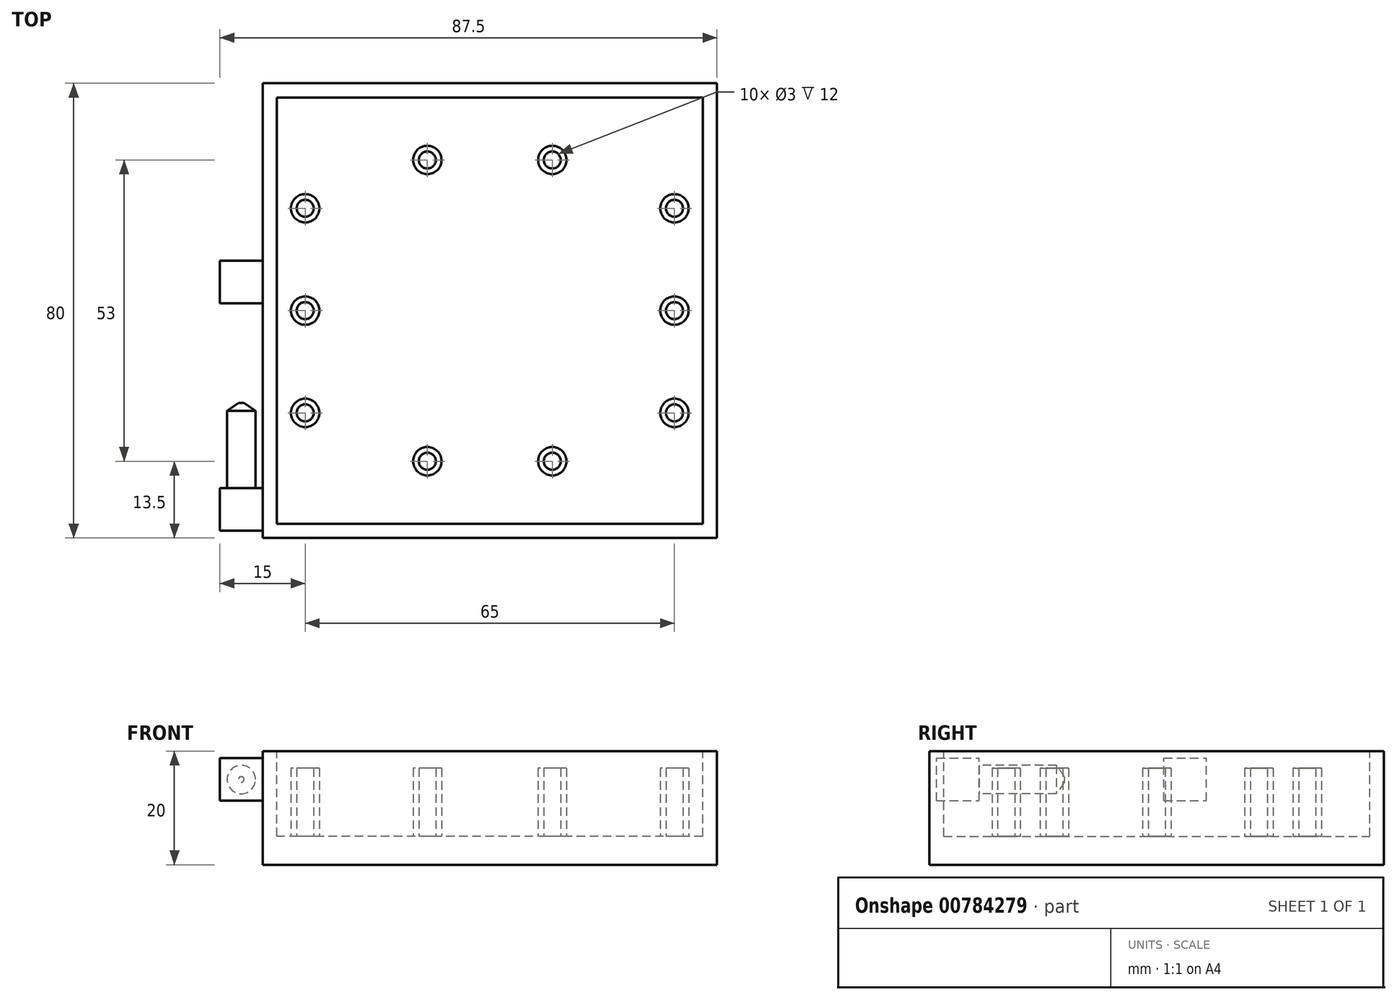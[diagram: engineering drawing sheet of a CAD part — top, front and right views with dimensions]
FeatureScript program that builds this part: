
annotation { "Feature Type Name" : "Feature", "Feature Type Description" : "" }
export const myFeature = defineFeature(function(context is Context, id is Id, definition is map)
    precondition{}
    {
        {
            var Q0;
            Q0=qCreatedBy(makeId("Top.planeOp"),FACE);
            var sketch = newSketch(context, id + "F0", { "sketchPlane" : qUnion([Q0])});
            skLineSegment(sketch, "E0.bottom", {"start": v(-40, -40) * mm, "end": v(40, -40) * mm});
            skLineSegment(sketch, "E0.top", {"start": v(-40, 40) * mm, "end": v(40, 40) * mm});
            skLineSegment(sketch, "E0.left", {"start": v(-40, -40) * mm, "end": v(-40, 40) * mm});
            skLineSegment(sketch, "E0.right", {"start": v(40, -40) * mm, "end": v(40, 40) * mm});
            skPoint(sketch, "E0.middle", {"position": v(0, 0) * mm});
            skSolve(sketch);
        }
        {
            var Q0;
            Q0=makeQuery(id+"F0.imprint","IMPRINT",FACE,{"disambiguationData":[TD([[makeQuery(id+"F0.imprint","IMPRINT",EDGE,{"derivedFrom":sQuery(id+"F0.wireOp",EDGE,"E0.bottom")}),1.0]])]});
            extrude(context, id + "F1", {"entities" : qUnion([Q0]), "depth" : 20 * mm, "offsetDistance" : 25 * mm});
        }
        {
            var Q0;
            Q0=makeQuery(id+"F1.opExtrude","CAP_FACE",FACE,{"disambiguationData":[OSD([sQuery(id+"F0.wireOp",EDGE,"E0.bottom"),sQuery(id+"F0.wireOp",EDGE,"E0.top"),sQuery(id+"F0.wireOp",EDGE,"E0.left"),sQuery(id+"F0.wireOp",EDGE,"E0.right")])],"isStart":false});
            var sketch = newSketch(context, id + "F2", { "sketchPlane" : qUnion([Q0])});
            skLineSegment(sketch, "E1.bottom", {"start": v(37.5, -37.5) * mm, "end": v(-37.5, -37.5) * mm});
            skLineSegment(sketch, "E1.top", {"start": v(37.5, 37.5) * mm, "end": v(-37.5, 37.5) * mm});
            skLineSegment(sketch, "E1.left", {"start": v(37.5, -37.5) * mm, "end": v(37.5, 37.5) * mm});
            skLineSegment(sketch, "E1.right", {"start": v(-37.5, -37.5) * mm, "end": v(-37.5, 37.5) * mm});
            skPoint(sketch, "E1.middle", {"position": v(0, 0) * mm});
            skSolve(sketch);
        }
        {
            var Q0;
            Q0=makeQuery(id+"F2.imprint","IMPRINT",FACE,{"disambiguationData":[TD([[makeQuery(id+"F2.imprint","IMPRINT",EDGE,{"derivedFrom":sQuery(id+"F2.wireOp",EDGE,"E1.bottom")}),-1.0]])]});
            extrude(context, id + "F3", {"entities" : qUnion([Q0]), "operationType" : NewBodyOperationType.REMOVE, "depth" : -15 * mm, "offsetDistance" : 25 * mm});
        }
        {
            var Q0;
            Q0=makeQuery(id+"F3.boolean.opBoolean","COPY",FACE,{"derivedFrom":makeQuery(id+"F3.opExtrude","CAP_FACE",FACE,{"disambiguationData":[OSD([sQuery(id+"F2.wireOp",EDGE,"E1.bottom"),sQuery(id+"F2.wireOp",EDGE,"E1.top"),sQuery(id+"F2.wireOp",EDGE,"E1.left"),sQuery(id+"F2.wireOp",EDGE,"E1.right")])],"isStart":false})});
            var sketch = newSketch(context, id + "F4", { "sketchPlane" : qUnion([Q0])});
            skLineSegment(sketch, "E2", {"start": v(-66.36, -26.5) * mm, "end": v(65.7, -26.5) * mm, "construction": true});
            skLineSegment(sketch, "E3", {"start": v(-32.5, -44) * mm, "end": v(-32.5, 44) * mm, "construction": true});
            skLineSegment(sketch, "E4", {"start": v(32.5, 44.96) * mm, "end": v(32.5, -44) * mm, "construction": true});
            skLineSegment(sketch, "E5", {"start": v(47.78, 26.5) * mm, "end": v(-45.97, 26.5) * mm, "construction": true});
            skCircle(sketch, "E6", {"center": v(-11, 26.5) * mm, "radius": 2.5 * mm});
            skCircle(sketch, "E7", {"center": v(11, 26.5) * mm, "radius": 2.5 * mm});
            skCircle(sketch, "E8", {"center": v(-11, -26.5) * mm, "radius": 2.5 * mm});
            skCircle(sketch, "E9", {"center": v(11, -26.5) * mm, "radius": 2.5 * mm});
            skCircle(sketch, "E10", {"center": v(-32.5, 18) * mm, "radius": 2.5 * mm});
            skCircle(sketch, "E11", {"center": v(-32.5, 0) * mm, "radius": 2.5 * mm});
            skCircle(sketch, "E12", {"center": v(-32.5, -18) * mm, "radius": 2.5 * mm});
            skLineSegment(sketch, "E13", {"start": v(-32.5, -18) * mm, "end": v(32.5, -18) * mm, "construction": true});
            skLineSegment(sketch, "E14", {"start": v(-32.5, 18) * mm, "end": v(32.5, 18) * mm, "construction": true});
            skLineSegment(sketch, "E15", {"start": v(-32.5, 0) * mm, "end": v(32.5, 0) * mm, "construction": true});
            skPoint(sketch, "E15.endSnap0", {"position": v(32.5, 0.48) * mm});
            skCircle(sketch, "E16", {"center": v(32.5, 18) * mm, "radius": 2.5 * mm});
            skCircle(sketch, "E17", {"center": v(32.5, 0) * mm, "radius": 2.5 * mm});
            skCircle(sketch, "E18", {"center": v(32.5, -18) * mm, "radius": 2.5 * mm});
            skCircle(sketch, "E19", {"center": v(32.5, -18) * mm, "radius": 1.5 * mm});
            skCircle(sketch, "E20", {"center": v(32.5, 0) * mm, "radius": 1.5 * mm});
            skCircle(sketch, "E21", {"center": v(11, -26.5) * mm, "radius": 1.5 * mm});
            skCircle(sketch, "E22", {"center": v(-11, -26.5) * mm, "radius": 1.5 * mm});
            skCircle(sketch, "E23", {"center": v(-32.5, -18) * mm, "radius": 1.5 * mm});
            skCircle(sketch, "E24", {"center": v(-32.5, 0) * mm, "radius": 1.5 * mm});
            skCircle(sketch, "E25", {"center": v(-32.5, 18) * mm, "radius": 1.5 * mm});
            skCircle(sketch, "E26", {"center": v(-11, 26.5) * mm, "radius": 1.5 * mm});
            skCircle(sketch, "E27", {"center": v(11, 26.5) * mm, "radius": 1.5 * mm});
            skCircle(sketch, "E28", {"center": v(32.5, 18) * mm, "radius": 1.5 * mm});
            skSolve(sketch);
        }
        {
            var Q0;
            Q0=makeQuery(id+"F4.imprint","IMPRINT",FACE,{"disambiguationData":[TD([[makeQuery(id+"F4.imprint","IMPRINT",EDGE,{"derivedFrom":sQuery(id+"F4.wireOp",EDGE,"E6")}),1.0]])]});
            var Q1;
            Q1=makeQuery(id+"F4.imprint","IMPRINT",FACE,{"disambiguationData":[TD([[makeQuery(id+"F4.imprint","IMPRINT",EDGE,{"derivedFrom":sQuery(id+"F4.wireOp",EDGE,"E7")}),1.0]])]});
            var Q2;
            Q2=makeQuery(id+"F4.imprint","IMPRINT",FACE,{"disambiguationData":[TD([[makeQuery(id+"F4.imprint","IMPRINT",EDGE,{"derivedFrom":sQuery(id+"F4.wireOp",EDGE,"E8")}),1.0]])]});
            var Q3;
            Q3=makeQuery(id+"F4.imprint","IMPRINT",FACE,{"disambiguationData":[TD([[makeQuery(id+"F4.imprint","IMPRINT",EDGE,{"derivedFrom":sQuery(id+"F4.wireOp",EDGE,"E9")}),1.0]])]});
            var Q4;
            Q4=makeQuery(id+"F4.imprint","IMPRINT",FACE,{"disambiguationData":[TD([[makeQuery(id+"F4.imprint","IMPRINT",EDGE,{"derivedFrom":sQuery(id+"F4.wireOp",EDGE,"E10")}),1.0]])]});
            var Q5;
            Q5=makeQuery(id+"F4.imprint","IMPRINT",FACE,{"disambiguationData":[TD([[makeQuery(id+"F4.imprint","IMPRINT",EDGE,{"derivedFrom":sQuery(id+"F4.wireOp",EDGE,"E11")}),1.0]])]});
            var Q6;
            Q6=makeQuery(id+"F4.imprint","IMPRINT",FACE,{"disambiguationData":[TD([[makeQuery(id+"F4.imprint","IMPRINT",EDGE,{"derivedFrom":sQuery(id+"F4.wireOp",EDGE,"E12")}),1.0]])]});
            var Q7;
            Q7=makeQuery(id+"F4.imprint","IMPRINT",FACE,{"disambiguationData":[TD([[makeQuery(id+"F4.imprint","IMPRINT",EDGE,{"derivedFrom":sQuery(id+"F4.wireOp",EDGE,"E17")}),1.0]])]});
            var Q8;
            Q8=makeQuery(id+"F4.imprint","IMPRINT",FACE,{"disambiguationData":[TD([[makeQuery(id+"F4.imprint","IMPRINT",EDGE,{"derivedFrom":sQuery(id+"F4.wireOp",EDGE,"E18")}),1.0]])]});
            var Q9;
            Q9=makeQuery(id+"F4.imprint","IMPRINT",FACE,{"disambiguationData":[TD([[makeQuery(id+"F4.imprint","IMPRINT",EDGE,{"derivedFrom":sQuery(id+"F4.wireOp",EDGE,"E16")}),1.0]])]});
            extrude(context, id + "F5", {"entities" : qUnion([Q0, Q1, Q2, Q3, Q4, Q5, Q6, Q7, Q8, Q9]), "operationType" : NewBodyOperationType.ADD, "depth" : 12 * mm, "offsetDistance" : 25 * mm});
        }
        {
            var Q0;
            Q0=makeQuery(id+"F1.opExtrude","SWEPT_FACE",FACE,{"disambiguationData":[OSD([sQuery(id+"F0.wireOp",EDGE,"E0.left")])]});
            var sketch = newSketch(context, id + "F6", { "sketchPlane" : qUnion([Q0])});
            skLineSegment(sketch, "E29", {"start": v(-39.04, 15) * mm, "end": v(35.89, 15) * mm, "construction": true});
            skLineSegment(sketch, "E30", {"start": v(35, 25.7) * mm, "end": v(35, -1.32) * mm, "construction": true});
            skLineSegment(sketch, "E31", {"start": v(-5, -3.64) * mm, "end": v(-5, 22.53) * mm, "construction": true});
            skLineSegment(sketch, "E32.bottom", {"start": v(-1.25, 11.25) * mm, "end": v(-8.75, 11.25) * mm});
            skLineSegment(sketch, "E32.top", {"start": v(-1.25, 18.75) * mm, "end": v(-8.75, 18.75) * mm});
            skLineSegment(sketch, "E32.left", {"start": v(-1.25, 11.25) * mm, "end": v(-1.25, 18.75) * mm});
            skLineSegment(sketch, "E32.right", {"start": v(-8.75, 11.25) * mm, "end": v(-8.75, 18.75) * mm});
            skPoint(sketch, "E32.middle", {"position": v(-5, 15) * mm});
            skLineSegment(sketch, "E33.bottom", {"start": v(38.75, 11.25) * mm, "end": v(31.25, 11.25) * mm});
            skLineSegment(sketch, "E33.top", {"start": v(38.75, 18.75) * mm, "end": v(31.25, 18.75) * mm});
            skLineSegment(sketch, "E33.left", {"start": v(38.75, 11.25) * mm, "end": v(38.75, 18.75) * mm});
            skLineSegment(sketch, "E33.right", {"start": v(31.25, 11.25) * mm, "end": v(31.25, 18.75) * mm});
            skPoint(sketch, "E33.middle", {"position": v(35, 15) * mm});
            skSolve(sketch);
        }
        {
            var Q0;
            Q0=makeQuery(id+"F6.imprint","IMPRINT",FACE,{"disambiguationData":[TD([[makeQuery(id+"F6.imprint","IMPRINT",EDGE,{"derivedFrom":sQuery(id+"F6.wireOp",EDGE,"E33.bottom")}),-1.0]])]});
            var Q1;
            Q1=makeQuery(id+"F6.imprint","IMPRINT",FACE,{"disambiguationData":[TD([[makeQuery(id+"F6.imprint","IMPRINT",EDGE,{"derivedFrom":sQuery(id+"F6.wireOp",EDGE,"E32.bottom")}),-1.0]])]});
            extrude(context, id + "F7", {"entities" : qUnion([Q0, Q1]), "operationType" : NewBodyOperationType.ADD, "depth" : 7.5 * mm, "offsetDistance" : 25 * mm});
        }
        {
            var Q0;
            Q0=makeQuery(id+"F7.opExtrude","SWEPT_FACE",FACE,{"disambiguationData":[OSD([sQuery(id+"F6.wireOp",EDGE,"E33.right")])]});
            var sketch = newSketch(context, id + "F8", { "sketchPlane" : qUnion([Q0])});
            skLineSegment(sketch, "E34", {"start": v(47.5, 15) * mm, "end": v(40, 15) * mm, "construction": true});
            skCircle(sketch, "E35", {"center": v(43.75, 15) * mm, "radius": 2.5 * mm});
            skSolve(sketch);
        }
        {
            var Q0;
            Q0=makeQuery(id+"F8.imprint","IMPRINT",FACE,{"disambiguationData":[TD([[makeQuery(id+"F8.imprint","IMPRINT",EDGE,{"derivedFrom":sQuery(id+"F8.wireOp",EDGE,"E35")}),1.0]])]});
            var Q1;
            Q1=sQuery(id+"F8.wireOp",EDGE,"E35");
            extrude(context, id + "F9", {"entities" : qUnion([Q0]), "operationType" : NewBodyOperationType.ADD, "surfaceEntities" : qUnion([Q1]), "depth" : 15 * mm, "offsetDistance" : 25 * mm});
        }
        {
            var Q0;
            Q0=makeQuery(id+"F9.opExtrude","CAP_EDGE",EDGE,{"disambiguationData":[OSD([sQuery(id+"F8.wireOp",EDGE,"E35")])],"isStart":false});
            chamfer(context, id + "F10", {"entities" : qUnion([Q0]), "chamferType" : ChamferType.OFFSET_ANGLE, "width" : 2 * mm, "oppositeDirection" : false, "angle" : 35 * degree, "tangentPropagation" : true});
        }
    });
